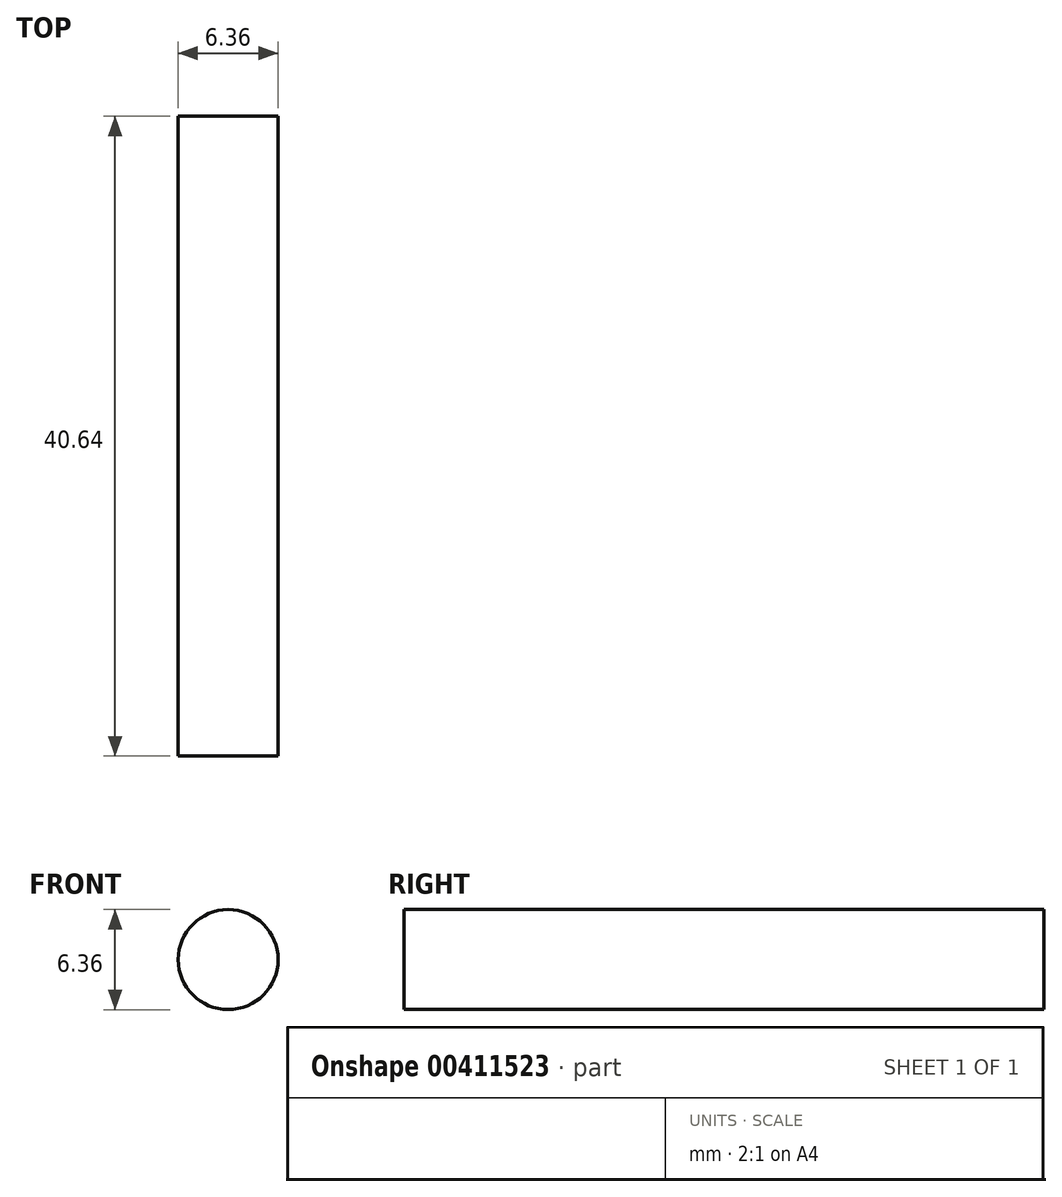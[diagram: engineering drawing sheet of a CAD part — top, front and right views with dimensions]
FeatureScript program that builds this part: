
annotation { "Feature Type Name" : "Feature", "Feature Type Description" : "" }
export const myFeature = defineFeature(function(context is Context, id is Id, definition is map)
    precondition{}
    {
        {
            var Q0;
            Q0=qCreatedBy(makeId("Front.planeOp"),FACE);
            var sketch = newSketch(context, id + "F0", { "sketchPlane" : qUnion([Q0])});
            skCircle(sketch, "E0", {"center": v(0, 0) * mm, "radius": 3.18 * mm});
            skSolve(sketch);
        }
        {
            var Q0;
            Q0 = qSketchRegion(id + "F0", true);
            extrude(context, id + "F1", {"entities" : qUnion([Q0]), "depth" : 40.64 * mm, "offsetDistance" : 25.4 * mm});
        }
    });
